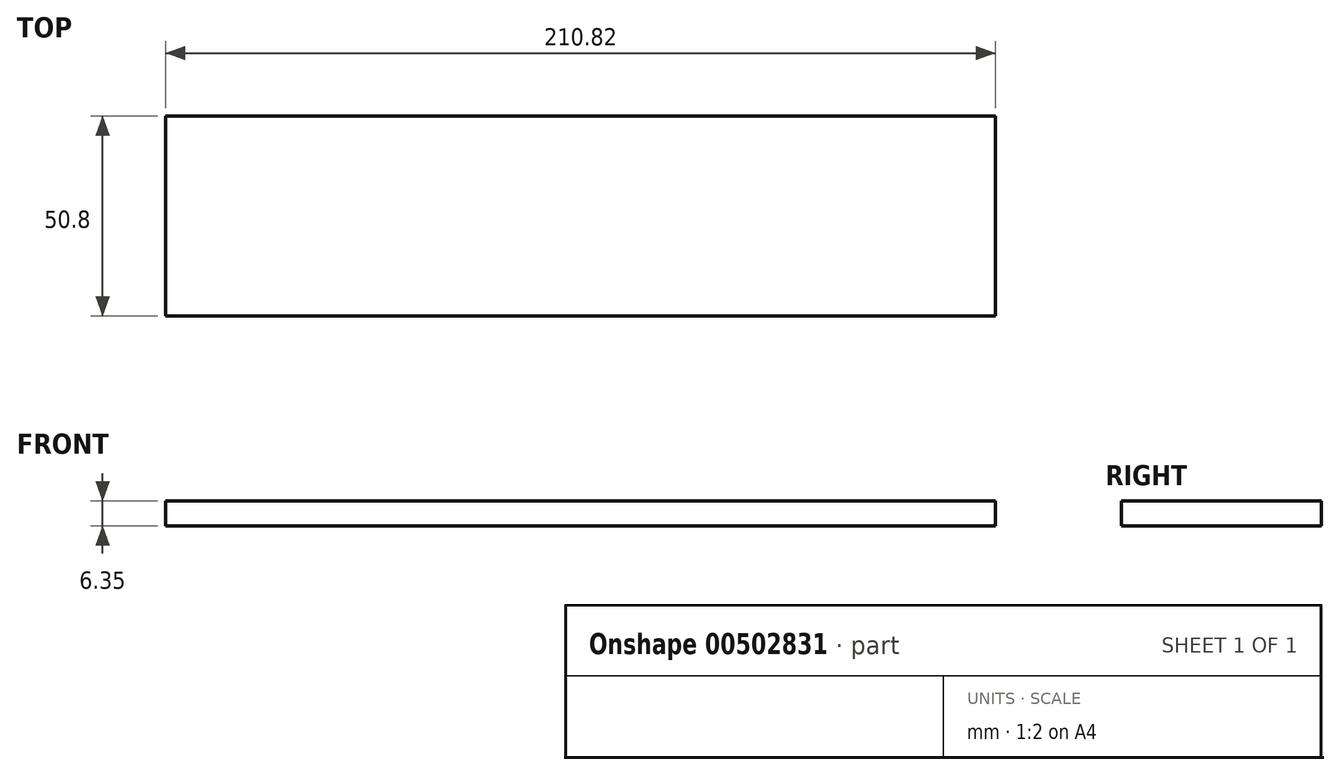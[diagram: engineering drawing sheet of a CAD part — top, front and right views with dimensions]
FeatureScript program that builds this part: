
annotation { "Feature Type Name" : "Feature", "Feature Type Description" : "" }
export const myFeature = defineFeature(function(context is Context, id is Id, definition is map)
    precondition{}
    {
        {
            var Q0;
            Q0=qCreatedBy(makeId("Top.planeOp"),FACE);
            var sketch = newSketch(context, id + "F0", { "sketchPlane" : qUnion([Q0])});
            skLineSegment(sketch, "E0.bottom", {"start": v(0, 0) * mm, "end": v(210.82, 0) * mm});
            skLineSegment(sketch, "E0.top", {"start": v(0, -50.8) * mm, "end": v(210.82, -50.8) * mm});
            skLineSegment(sketch, "E0.left", {"start": v(0, 0) * mm, "end": v(0, -50.8) * mm});
            skLineSegment(sketch, "E0.right", {"start": v(210.82, 0) * mm, "end": v(210.82, -50.8) * mm});
            skSolve(sketch);
        }
        {
            var Q0;
            Q0=makeQuery(id+"F0.imprint","IMPRINT",FACE,{"disambiguationData":[TD([[makeQuery(id+"F0.imprint","IMPRINT",EDGE,{"derivedFrom":sQuery(id+"F0.wireOp",EDGE,"E0.bottom")}),-1.0]])]});
            extrude(context, id + "F1", {"entities" : qUnion([Q0]), "depth" : 6.35 * mm, "offsetDistance" : 25.4 * mm});
        }
    });
